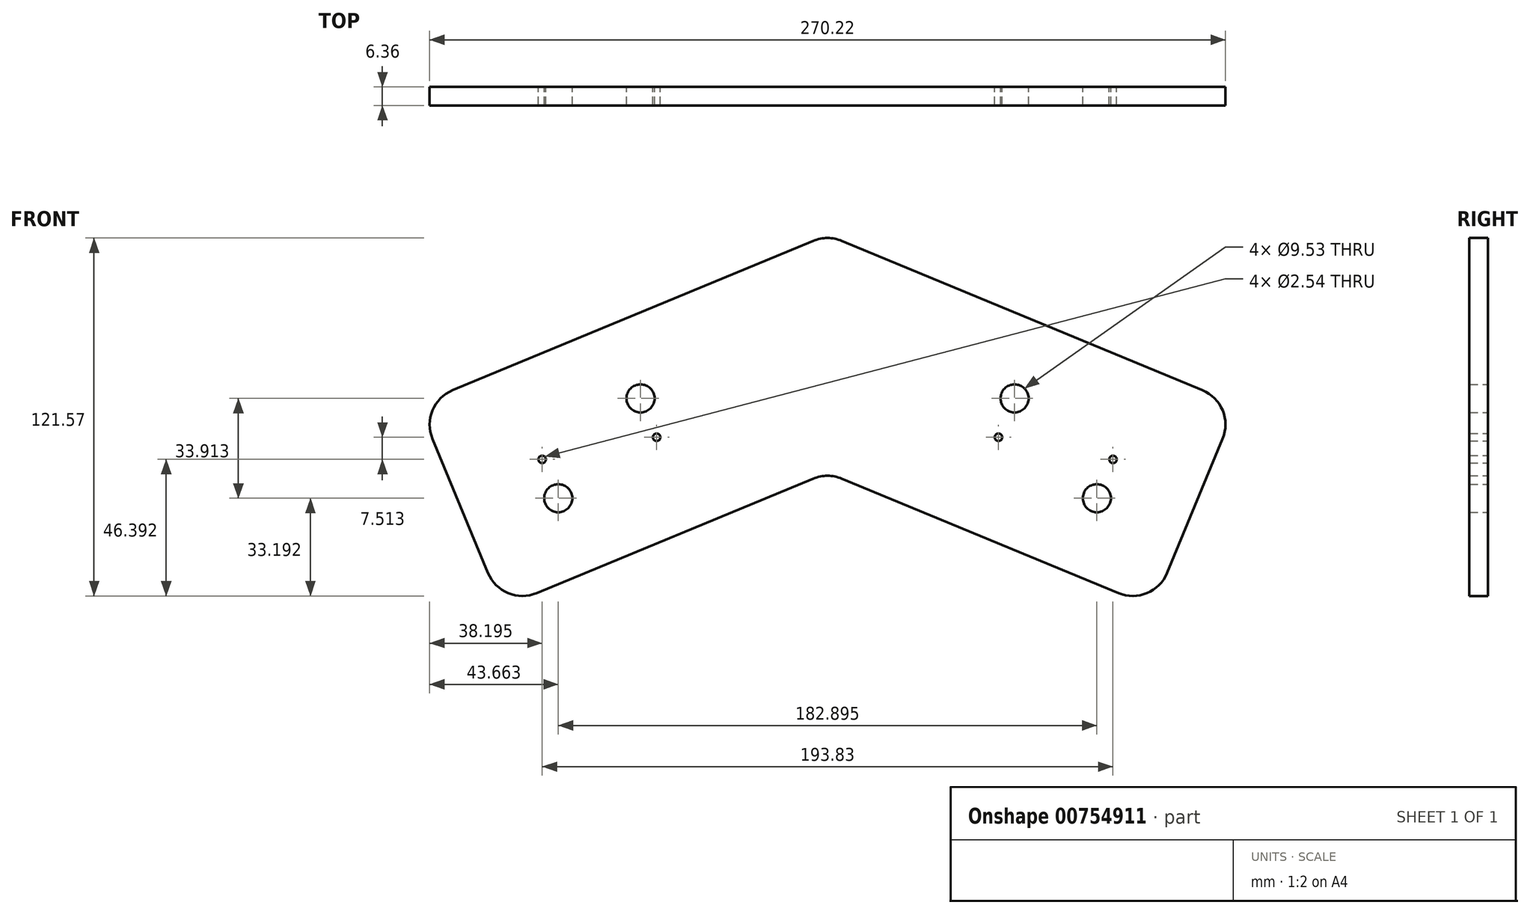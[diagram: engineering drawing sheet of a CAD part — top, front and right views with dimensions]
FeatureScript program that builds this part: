
annotation { "Feature Type Name" : "Feature", "Feature Type Description" : "" }
export const myFeature = defineFeature(function(context is Context, id is Id, definition is map)
    precondition{}
    {
        {
            var Q0;
            Q0=qCreatedBy(makeId("Front.planeOp"),FACE);
            var sketch = newSketch(context, id + "F0", { "sketchPlane" : qUnion([Q0])});
            skLineSegment(sketch, "E0", {"start": v(0, 0) * mm, "end": v(-110.45, -45.75) * mm});
            skLineSegment(sketch, "E1", {"start": v(0, 0) * mm, "end": v(0, 80.76) * mm});
            skLineSegment(sketch, "E2", {"start": v(-110.45, -45.75) * mm, "end": v(-139, 23.18) * mm});
            skLineSegment(sketch, "E3", {"start": v(-139, 23.18) * mm, "end": v(0, 80.76) * mm});
            skPoint(sketch, "E4", {"position": v(-15.88, 84.5) * mm});
            skPoint(sketch, "E5", {"position": v(-15.88, -16.89) * mm});
            skLineSegment(sketch, "E6.MirrorCS", {"start": v(0, 0) * mm, "end": v(110.45, -45.75) * mm});
            skPoint(sketch, "E7.MirrorP", {"position": v(15.88, -16.89) * mm});
            skLineSegment(sketch, "E8.MirrorCS", {"start": v(110.45, -45.75) * mm, "end": v(139, 23.18) * mm});
            skLineSegment(sketch, "E9.MirrorCS", {"start": v(139, 23.18) * mm, "end": v(0, 80.76) * mm});
            skPoint(sketch, "E10.MirrorP", {"position": v(15.88, 84.5) * mm});
            skLineSegment(sketch, "E11", {"start": v(-15.87, -16.89) * mm, "end": v(-45.04, 53.51) * mm, "construction": true});
            skLineSegment(sketch, "E12", {"start": v(-15.88, 84.5) * mm, "end": v(13.29, 14.1) * mm, "construction": true});
            skCircle(sketch, "E13", {"center": v(-91.45, -8.67) * mm, "radius": 4.76 * mm});
            skLineSegment(sketch, "E14", {"start": v(-91.45, -8.67) * mm, "end": v(-109.67, 35.33) * mm, "construction": true});
            skCircle(sketch, "E15.MirrorC", {"center": v(91.45, -8.67) * mm, "radius": 4.76 * mm});
            skCircle(sketch, "E16", {"center": v(-63.5, 25.25) * mm, "radius": 4.76 * mm});
            skLineSegment(sketch, "E17", {"start": v(-63.5, 25.25) * mm, "end": v(-45.28, -18.75) * mm});
            skCircle(sketch, "E18.MirrorC", {"center": v(63.5, 25.25) * mm, "radius": 4.76 * mm});
            skCircle(sketch, "E19", {"center": v(-58.03, 12.05) * mm, "radius": 1.27 * mm});
            skCircle(sketch, "E20", {"center": v(-96.91, 4.53) * mm, "radius": 1.27 * mm});
            skCircle(sketch, "E21.MirrorC", {"center": v(58.03, 12.05) * mm, "radius": 1.27 * mm});
            skCircle(sketch, "E22.MirrorC", {"center": v(96.91, 4.53) * mm, "radius": 1.27 * mm});
            skPoint(sketch, "E23", {"position": v(-100.56, 13.33) * mm});
            skSolve(sketch);
        }
        {
            var Q0;
            Q0=qSketchRegion(id+"F0",true);
            extrude(context, id + "F1", {"entities" : qUnion([Q0]), "endBound" : BoundingType.SYMMETRIC, "depth" : 6.35 * mm, "offsetDistance" : 25.4 * mm});
        }
        {
            var Q0;
            Q0=makeQuery(id+"F1.opExtrude","SWEPT_EDGE",EDGE,{"disambiguationData":[OSD([sQuery(id+"F0.wireOp",EDGE,"E2"),sQuery(id+"F0.wireOp",EDGE,"E3")])]});
            var Q1;
            Q1=makeQuery(id+"F1.opExtrude","SWEPT_EDGE",EDGE,{"disambiguationData":[OSD([sQuery(id+"F0.wireOp",EDGE,"E3"),sQuery(id+"F0.wireOp",EDGE,"E1"),sQuery(id+"F0.wireOp",EDGE,"E9.MirrorCS")])]});
            var Q2;
            Q2=makeQuery(id+"F1.opExtrude","SWEPT_EDGE",EDGE,{"disambiguationData":[OSD([sQuery(id+"F0.wireOp",EDGE,"E0"),sQuery(id+"F0.wireOp",EDGE,"E6.MirrorCS"),sQuery(id+"F0.wireOp",EDGE,"E1")])]});
            var Q3;
            Q3=makeQuery(id+"F1.opExtrude","SWEPT_EDGE",EDGE,{"disambiguationData":[OSD([sQuery(id+"F0.wireOp",EDGE,"E6.MirrorCS"),sQuery(id+"F0.wireOp",EDGE,"E8.MirrorCS")])]});
            var Q4;
            Q4=makeQuery(id+"F1.opExtrude","SWEPT_EDGE",EDGE,{"disambiguationData":[OSD([sQuery(id+"F0.wireOp",EDGE,"E8.MirrorCS"),sQuery(id+"F0.wireOp",EDGE,"E9.MirrorCS")])]});
            var Q5;
            Q5=makeQuery(id+"F1.opExtrude","SWEPT_EDGE",EDGE,{"disambiguationData":[OSD([sQuery(id+"F0.wireOp",EDGE,"E0"),sQuery(id+"F0.wireOp",EDGE,"E2")])]});
            fillet(context, id + "F2", {"entities" : qUnion([Q0, Q1, Q2, Q3, Q4, Q5]), "radius" : 12.7 * mm, "tangentPropagation" : true, "allowEdgeOverflow" : false});
        }
    });
